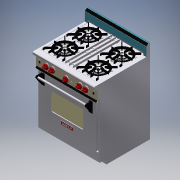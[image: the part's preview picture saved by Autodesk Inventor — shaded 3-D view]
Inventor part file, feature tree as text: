
AUTODESK INVENTOR PART (.ipt)
format: ipt  version: 2016 (Build 200138000, 138)  size: 20,739,072 bytes
history: native  units: in
note: dims shown in document units (in); Inventor stores cm internally (conversion verified against a paired STEP export)
features: fillet x5, imported_body x1
ambient origin geometry x8: Origin, YZ Plane, XZ Plane, XY Plane, X Axis, Y Axis, Z Axis, Center Point
bodies: Solid1 (feature_tree)
feature tree (6):
  imported_body  "Base1"
  fillet  "Fillet1"  Radius=0.0312in
  fillet  "Fillet2"  Radius=0.0312in
  fillet  "Fillet3"  Radius=0.0312in
  fillet  "Fillet4"  Radius=0.0312in
  fillet  "Fillet5"  Radius=0.0312in
